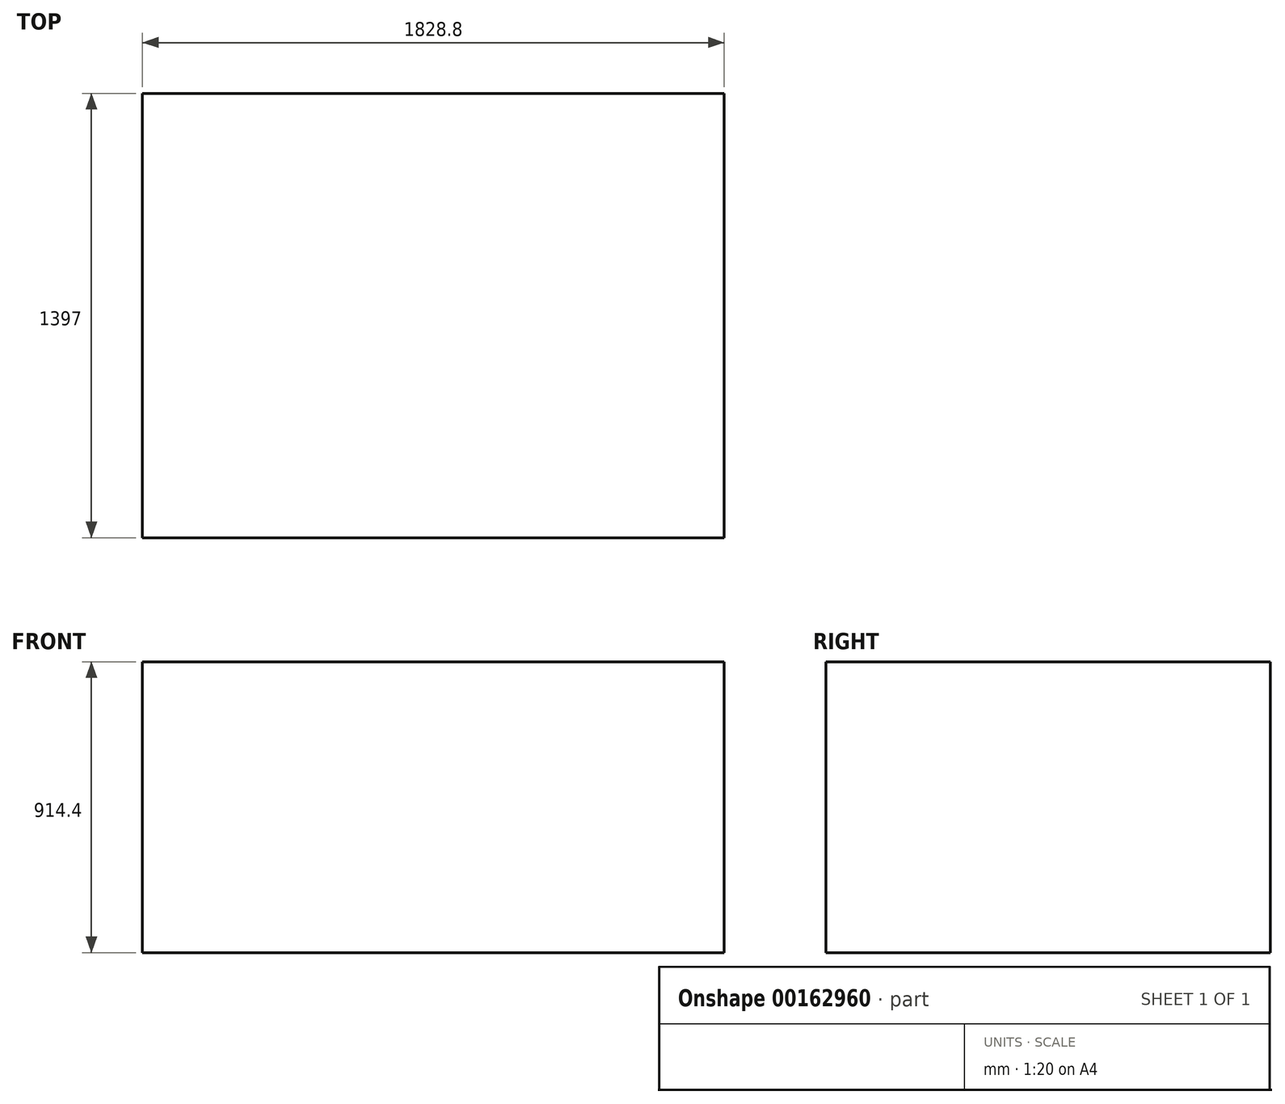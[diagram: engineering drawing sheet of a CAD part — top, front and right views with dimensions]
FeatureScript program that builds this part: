
annotation { "Feature Type Name" : "Feature", "Feature Type Description" : "" }
export const myFeature = defineFeature(function(context is Context, id is Id, definition is map)
    precondition{}
    {
        {
            var Q0;
            Q0=qCreatedBy(makeId("Top.planeOp"),FACE);
            var sketch = newSketch(context, id + "F0", { "sketchPlane" : qUnion([Q0])});
            skLineSegment(sketch, "E0.bottom", {"start": v(0, 0) * mm, "end": v(1828.8, 0) * mm});
            skLineSegment(sketch, "E0.top", {"start": v(0, 1397) * mm, "end": v(1828.8, 1397) * mm});
            skLineSegment(sketch, "E0.left", {"start": v(0, 0) * mm, "end": v(0, 1397) * mm});
            skLineSegment(sketch, "E0.right", {"start": v(1828.8, 0) * mm, "end": v(1828.8, 1397) * mm});
            skSolve(sketch);
        }
        {
            var Q0;
            Q0 = qSketchRegion(id + "F0", true);
            extrude(context, id + "F1", {"entities" : qUnion([Q0]), "depth" : 914.4 * mm});
        }
    });
